# Revit family: Lighting_Fixture-Wall-Astro-Domino
name_source: partatom
category: Lighting Fixtures
revit_build: Autodesk Revit 2014 (Build: 20130308_1515(x64)
units: mm (PartAtom-declared; Revit-internal decimal feet)

## types (1)
- 7392 Domino
    Apparent Load = 5 VA
    Assembly Code = D5020200
    Casing Material = Astro - Aluminium - Chrome Finish
    Class = 2
    Color Filter = 16777215
    Description = Mirror light
    Dimmable = No
    Dimming Lamp Color Temperature Shift = <None>
    Energy Efficiency Rating = A
    Height = 206 mm  [stored 0.675853 ft]
    IP Rating = IP44
    Lamp = LED
    Lamp included = Yes
    Length = 75 mm
    Light Source Elevation = 1680.5 mm  [stored 5.51345 ft]
    Light Source From Wall = 55 mm
    Luminaire Lamp Efficiency Rating = A
    Manufacturer = Astro Lighting Ltd, CM20 2DP
    Model = 7392 Domino
    Mountable on normally flammable surfaces = Yes
    Number of Poles = 1
    Photometric Web File = Astro P4558 PV Domino. 251114.IES
    Product Documentation = http://www.astrolighting.co.uk
products/kw/domino/7392_Domino
    Suitable for bathroom zone = Zone 2, 3
    Tilt Angle = 0.00°
    Type Comments = -Includes integral LED driver
    URL = www.astrolighting.co.uk
    Voltage = 230 V
    Wattage Comments = 3.6w
    Weight = 0.65 kg
    Width = 40 mm  [stored 0.131234 ft]

note: [stored X ft] marks values corroborated as IEEE doubles in the binary element streams (Revit-internal decimal feet)

## geometry (parser evidence)
native form markers: Sweep x6
no freeform markers — native parametric forms only
